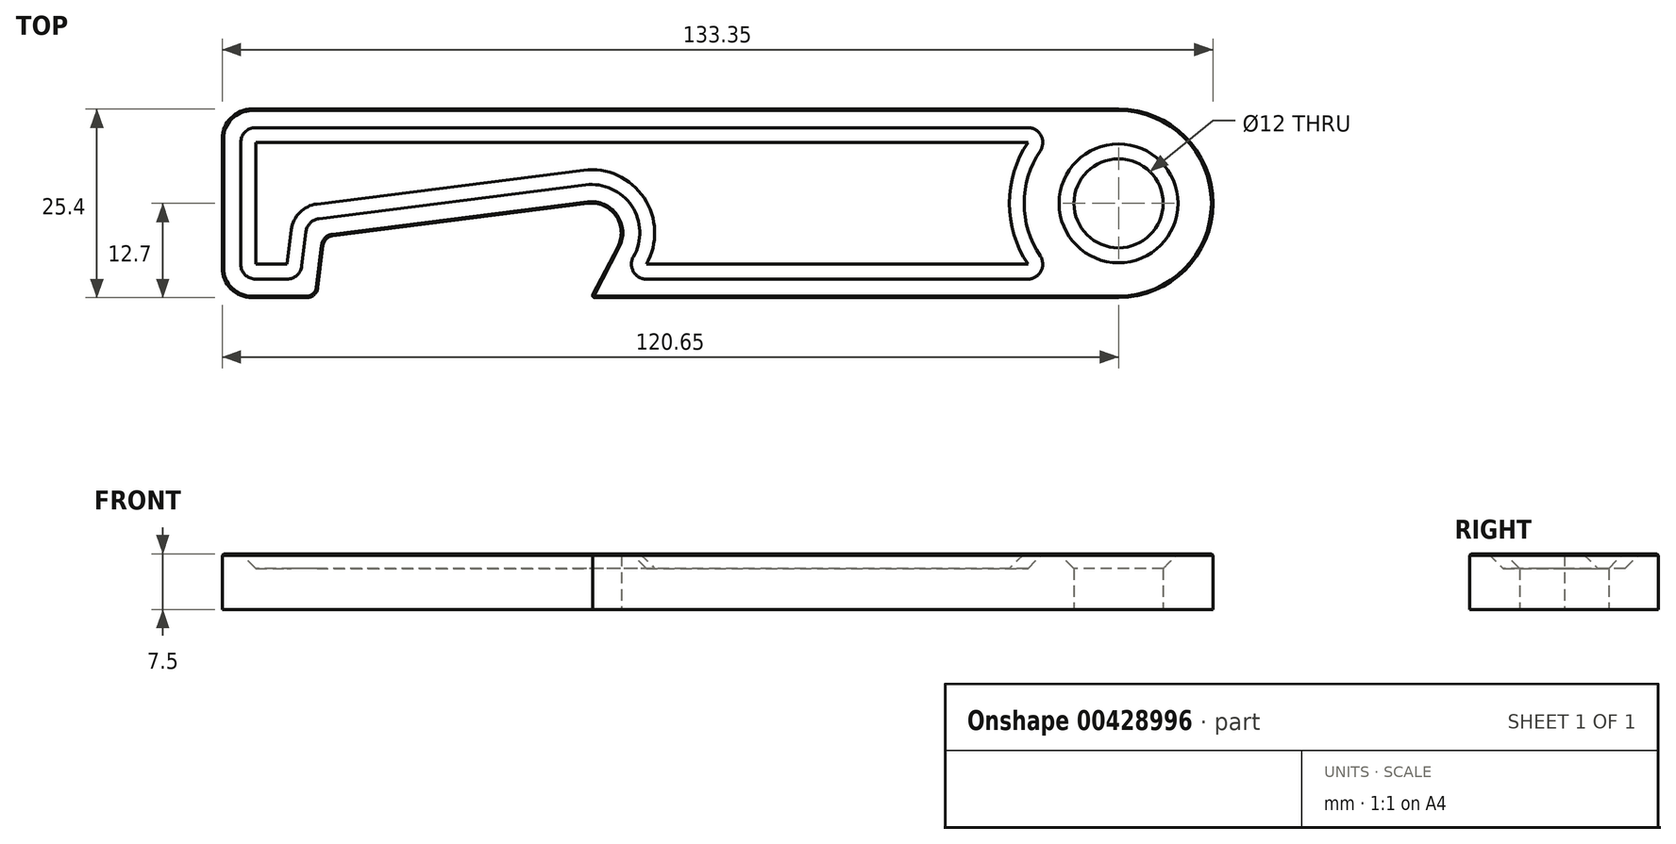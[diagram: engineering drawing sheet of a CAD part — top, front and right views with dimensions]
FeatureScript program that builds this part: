
annotation { "Feature Type Name" : "Feature", "Feature Type Description" : "" }
export const myFeature = defineFeature(function(context is Context, id is Id, definition is map)
    precondition{}
    {
        {
            var Q0;
            Q0=qCreatedBy(makeId("Top.planeOp"),FACE);
            var sketch = newSketch(context, id + "F0", { "sketchPlane" : qUnion([Q0])});
            skLineSegment(sketch, "E0.bottom", {"start": v(-116.65, 12.7) * mm, "end": v(0, 12.7) * mm});
            skLineSegment(sketch, "E0.top", {"start": v(-116.65, -12.7) * mm, "end": v(-109.28, -12.7) * mm});
            skLineSegment(sketch, "E0.left", {"start": v(-120.65, 8.7) * mm, "end": v(-120.65, -8.7) * mm});
            skArc(sketch, "E1", {"start": v(0, -12.7) * mm, "mid": v(12.7, 0) * mm, "end": v(0, 12.7) * mm});
            skPoint(sketch, "E2.visualSharp", {"position": v(-120.65, 12.7) * mm});
            skArc(sketch, "E2.filletArc", {"start": v(-116.65, 12.7) * mm, "mid": v(-119.48, 11.53) * mm, "end": v(-120.65, 8.7) * mm});
            skPoint(sketch, "E3.visualSharp", {"position": v(-120.65, -12.7) * mm});
            skArc(sketch, "E3.filletArc", {"start": v(-120.65, -8.7) * mm, "mid": v(-119.48, -11.53) * mm, "end": v(-116.65, -12.7) * mm});
            skCircle(sketch, "E4", {"center": v(0, 0) * mm, "radius": 6 * mm});
            skLineSegment(sketch, "E5", {"start": v(-107.79, -11.38) * mm, "end": v(-107.08, -5.66) * mm});
            skLineSegment(sketch, "E6", {"start": v(-105.78, -4.35) * mm, "end": v(-71.44, 0) * mm});
            skArc(sketch, "E7", {"start": v(-66.93, -3.97) * mm, "mid": v(-68.29, -0.97) * mm, "end": v(-71.44, 0) * mm});
            skLineSegment(sketch, "E8.trimOffspring", {"start": v(-70.52, -12.7) * mm, "end": v(0, -12.7) * mm});
            skArc(sketch, "E9", {"start": v(-67.38, -5.8) * mm, "mid": v(-67.66, -1.68) * mm, "end": v(-71.44, 0) * mm});
            skLineSegment(sketch, "E10", {"start": v(-67.38, -5.8) * mm, "end": v(-70.75, -12.34) * mm});
            skPoint(sketch, "E11.visualSharp", {"position": v(-107.95, -12.7) * mm});
            skArc(sketch, "E11.filletArc", {"start": v(-109.28, -12.7) * mm, "mid": v(-108.28, -12.32) * mm, "end": v(-107.79, -11.38) * mm});
            skPoint(sketch, "E12.visualSharp", {"position": v(-106.93, -4.5) * mm});
            skArc(sketch, "E12.filletArc", {"start": v(-105.78, -4.35) * mm, "mid": v(-106.65, -4.78) * mm, "end": v(-107.08, -5.66) * mm});
            skPoint(sketch, "E13.visualSharp", {"position": v(-70.93, -12.7) * mm});
            skArc(sketch, "E13.filletArc", {"start": v(-70.75, -12.34) * mm, "mid": v(-70.74, -12.58) * mm, "end": v(-70.52, -12.7) * mm});
            skSolve(sketch);
        }
        {
            var Q0;
            Q0=qSketchRegion(id+"F0",true);
            extrude(context, id + "F1", {"entities" : qUnion([Q0]), "depth" : 7.5 * mm});
        }
        {
            var Q0;
            Q0=makeQuery(id+"F1.opExtrude","CAP_FACE",FACE,{"disambiguationData":[OSD([sQuery(id+"F0.wireOp",EDGE,"E0.bottom"),sQuery(id+"F0.wireOp",EDGE,"E0.top"),sQuery(id+"F0.wireOp",EDGE,"E0.left"),sQuery(id+"F0.wireOp",EDGE,"E1"),sQuery(id+"F0.wireOp",EDGE,"E2.filletArc"),sQuery(id+"F0.wireOp",EDGE,"E3.filletArc"),sQuery(id+"F0.wireOp",EDGE,"E4"),sQuery(id+"F0.wireOp",EDGE,"E5"),sQuery(id+"F0.wireOp",EDGE,"E6"),sQuery(id+"F0.wireOp",EDGE,"E8.trimOffspring"),sQuery(id+"F0.wireOp",EDGE,"E9"),sQuery(id+"F0.wireOp",EDGE,"E10"),sQuery(id+"F0.wireOp",EDGE,"E11.filletArc"),sQuery(id+"F0.wireOp",EDGE,"E12.filletArc"),sQuery(id+"F0.wireOp",EDGE,"E13.filletArc")])],"isStart":false});
            var sketch = newSketch(context, id + "F2", { "sketchPlane" : qUnion([Q0])});
            skArc(sketch, "E14", {"start": v(-10.54, 7.08) * mm, "mid": v(-12.7, 0) * mm, "end": v(-10.54, -7.08) * mm});
            skArc(sketch, "E15", {"start": v(-116.15, 10.2) * mm, "mid": v(-117.56, 9.61) * mm, "end": v(-118.15, 8.2) * mm});
            skArc(sketch, "E16", {"start": v(-118.15, -8.2) * mm, "mid": v(-117.56, -9.61) * mm, "end": v(-116.15, -10.2) * mm});
            skLineSegment(sketch, "E17", {"start": v(-116.15, 10.2) * mm, "end": v(-12.2, 10.2) * mm});
            skLineSegment(sketch, "E18", {"start": v(-118.15, 8.2) * mm, "end": v(-118.15, -8.2) * mm});
            skLineSegment(sketch, "E19", {"start": v(-116.15, -10.2) * mm, "end": v(-111.93, -10.2) * mm});
            skLineSegment(sketch, "E20", {"start": v(-109.94, -8.45) * mm, "end": v(-109.37, -3.8) * mm});
            skPoint(sketch, "E21.visualSharp", {"position": v(-110.16, -10.2) * mm});
            skArc(sketch, "E21.filletArc", {"start": v(-111.93, -10.2) * mm, "mid": v(-110.6, -9.7) * mm, "end": v(-109.94, -8.45) * mm});
            skLineSegment(sketch, "E22", {"start": v(-109.56, -5.36) * mm, "end": v(-107.08, -5.66) * mm, "construction": true});
            skLineSegment(sketch, "E23", {"start": v(-114.04, -10.2) * mm, "end": v(-114.04, -12.7) * mm, "construction": true});
            skLineSegment(sketch, "E24", {"start": v(-118.15, 0) * mm, "end": v(-120.65, 0) * mm, "construction": true});
            skLineSegment(sketch, "E25", {"start": v(-58.33, 12.7) * mm, "end": v(-58.33, 10.2) * mm, "construction": true});
            skLineSegment(sketch, "E26", {"start": v(-107.63, -2.07) * mm, "end": v(-71.75, 2.48) * mm});
            skLineSegment(sketch, "E27", {"start": v(-88.6, -2.18) * mm, "end": v(-88.92, 0.3) * mm, "construction": true});
            skLineSegment(sketch, "E28", {"start": v(-111.93, -8.2) * mm, "end": v(-111.93, -10.2) * mm, "construction": true});
            skLineSegment(sketch, "E29", {"start": v(-116.15, -8.2) * mm, "end": v(-116.15, -10.2) * mm, "construction": true});
            skPoint(sketch, "E30.visualSharp", {"position": v(-109.18, -2.26) * mm});
            skArc(sketch, "E30.filletArc", {"start": v(-107.63, -2.07) * mm, "mid": v(-108.8, -2.64) * mm, "end": v(-109.37, -3.8) * mm});
            skArc(sketch, "E31", {"start": v(-65.3, -7.2) * mm, "mid": v(-65.53, -0.36) * mm, "end": v(-71.75, 2.48) * mm});
            skLineSegment(sketch, "E32", {"start": v(-74.21, -6.26) * mm, "end": v(-65.6, -0.24) * mm});
            skLineSegment(sketch, "E33", {"start": v(-65.6, -0.24) * mm, "end": v(-70.93, -3.97) * mm, "construction": true});
            skLineSegment(sketch, "E34", {"start": v(-63.56, -10.2) * mm, "end": v(-12.2, -10.2) * mm});
            skLineSegment(sketch, "E35", {"start": v(-35.26, -12.7) * mm, "end": v(-35.26, -10.2) * mm, "construction": true});
            skPoint(sketch, "E36.visualSharp", {"position": v(-69.09, -10.2) * mm});
            skArc(sketch, "E36.filletArc", {"start": v(-65.3, -7.2) * mm, "mid": v(-65.3, -9.2) * mm, "end": v(-63.56, -10.2) * mm});
            skPoint(sketch, "E37.visualSharp", {"position": v(-7.57, -10.2) * mm});
            skArc(sketch, "E37.filletArc", {"start": v(-12.2, -10.2) * mm, "mid": v(-10.44, -9.14) * mm, "end": v(-10.54, -7.08) * mm});
            skPoint(sketch, "E38.visualSharp", {"position": v(-7.57, 10.2) * mm});
            skArc(sketch, "E38.filletArc", {"start": v(-10.54, 7.08) * mm, "mid": v(-10.44, 9.14) * mm, "end": v(-12.2, 10.2) * mm});
            skLineSegment(sketch, "E39", {"start": v(0, 0) * mm, "end": v(-12.7, 0) * mm, "construction": true});
            skLineSegment(sketch, "E40", {"start": v(0, 0) * mm, "end": v(12.7, 0) * mm, "construction": true});
            skSolve(sketch);
        }
        {
            var Q0;
            Q0=qSketchRegion(id+"F2",true);
            extrude(context, id + "F3", {"entities" : qUnion([Q0]), "operationType" : NewBodyOperationType.REMOVE, "oppositeDirection" : true, "depth" : 2 * mm});
        }
        {
            var Q0;
            Q0=makeQuery(id+"F3.boolean.opBoolean","COPY",FACE,{"derivedFrom":makeQuery(id+"F3.opExtrude","CAP_FACE",FACE,{"disambiguationData":[OSD([sQuery(id+"F2.wireOp",EDGE,"E14"),sQuery(id+"F2.wireOp",EDGE,"E15"),sQuery(id+"F2.wireOp",EDGE,"E16"),sQuery(id+"F2.wireOp",EDGE,"E17"),sQuery(id+"F2.wireOp",EDGE,"E18"),sQuery(id+"F2.wireOp",EDGE,"E19"),sQuery(id+"F2.wireOp",EDGE,"E20"),sQuery(id+"F2.wireOp",EDGE,"E21.filletArc"),sQuery(id+"F2.wireOp",EDGE,"E26"),sQuery(id+"F2.wireOp",EDGE,"E30.filletArc"),sQuery(id+"F2.wireOp",EDGE,"E31"),sQuery(id+"F2.wireOp",EDGE,"E34"),sQuery(id+"F2.wireOp",EDGE,"E36.filletArc"),sQuery(id+"F2.wireOp",EDGE,"E37.filletArc"),sQuery(id+"F2.wireOp",EDGE,"E38.filletArc")])],"isStart":false})});
            chamfer(context, id + "F4", {"entities" : qUnion([Q0]), "width" : 2 * mm, "tangentPropagation" : true});
        }
        {
            var Q0;
            Q0=makeQuery(id+"F1.opExtrude","CAP_EDGE",EDGE,{"disambiguationData":[OSD([sQuery(id+"F0.wireOp",EDGE,"E4")])],"isStart":false});
            chamfer(context, id + "F5", {"entities" : qUnion([Q0]), "width" : 2 * mm, "tangentPropagation" : true});
        }
        {
            var Q0;
            Q0=makeQuery(id+"F1.opExtrude","CAP_EDGE",EDGE,{"disambiguationData":[OSD([sQuery(id+"F0.wireOp",EDGE,"E0.bottom")])],"isStart":false});
            chamfer(context, id + "F6", {"entities" : qUnion([Q0]), "width" : 0.2 * mm, "tangentPropagation" : true});
        }
    });
